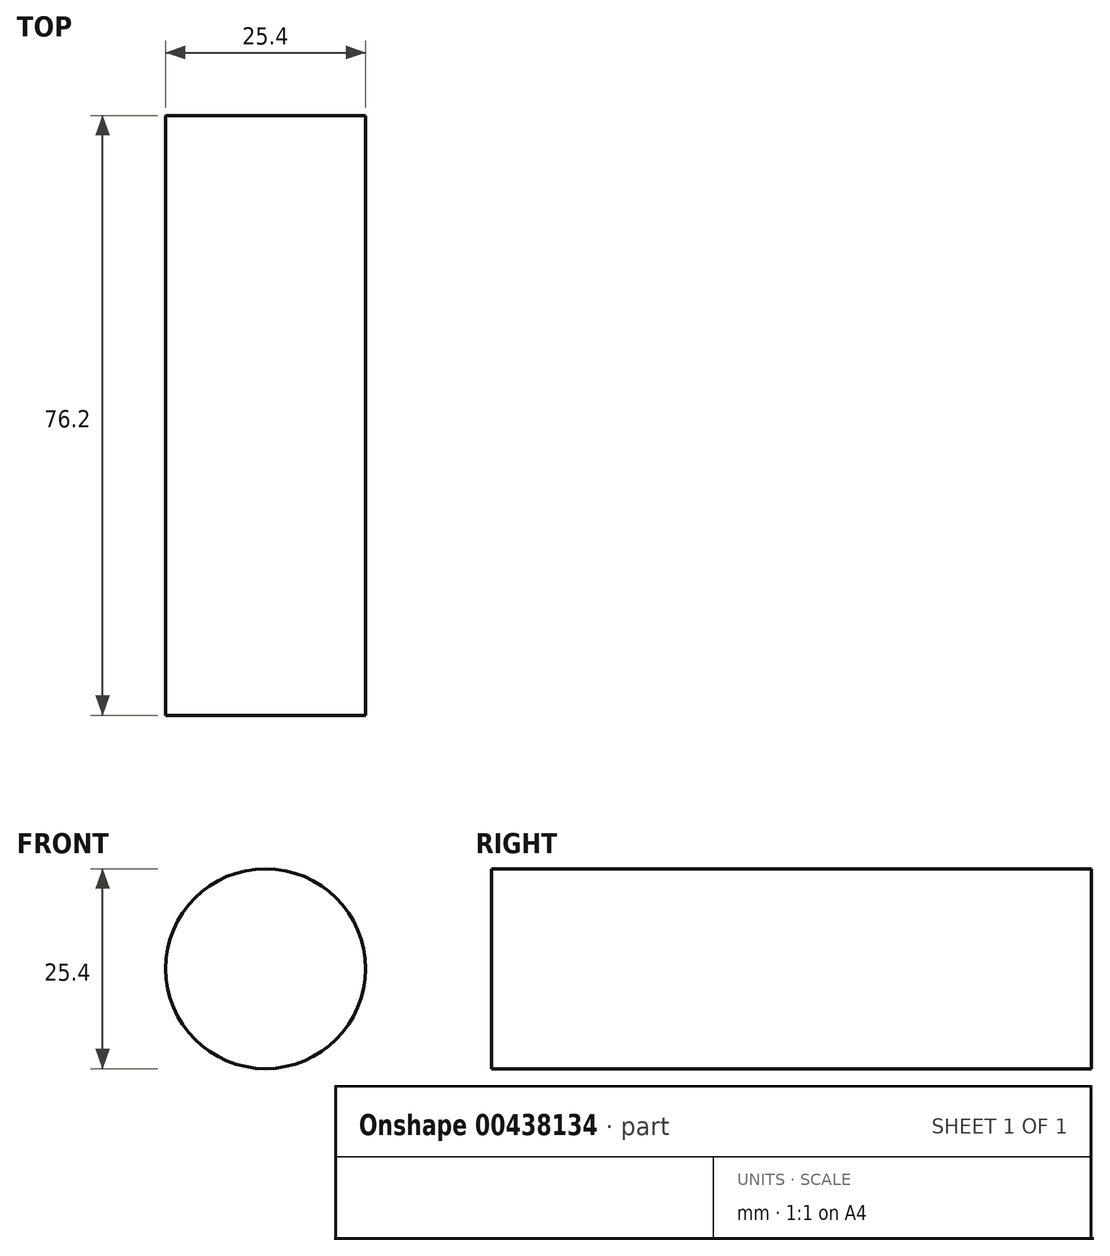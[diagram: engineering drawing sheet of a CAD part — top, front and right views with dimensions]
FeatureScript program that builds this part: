
annotation { "Feature Type Name" : "Feature", "Feature Type Description" : "" }
export const myFeature = defineFeature(function(context is Context, id is Id, definition is map)
    precondition{}
    {
        {
            var Q0;
            Q0=qCreatedBy(makeId("Front.planeOp"),FACE);
            var sketch = newSketch(context, id + "F0", { "sketchPlane" : qUnion([Q0])});
            skCircle(sketch, "E0", {"center": v(-24.25, 30.17) * mm, "radius": 12.7 * mm});
            skSolve(sketch);
        }
        {
            var Q0;
            Q0 = qSketchRegion(id + "F0", true);
            extrude(context, id + "F1", {"entities" : qUnion([Q0]), "depth" : 76.2 * mm});
        }
    });
